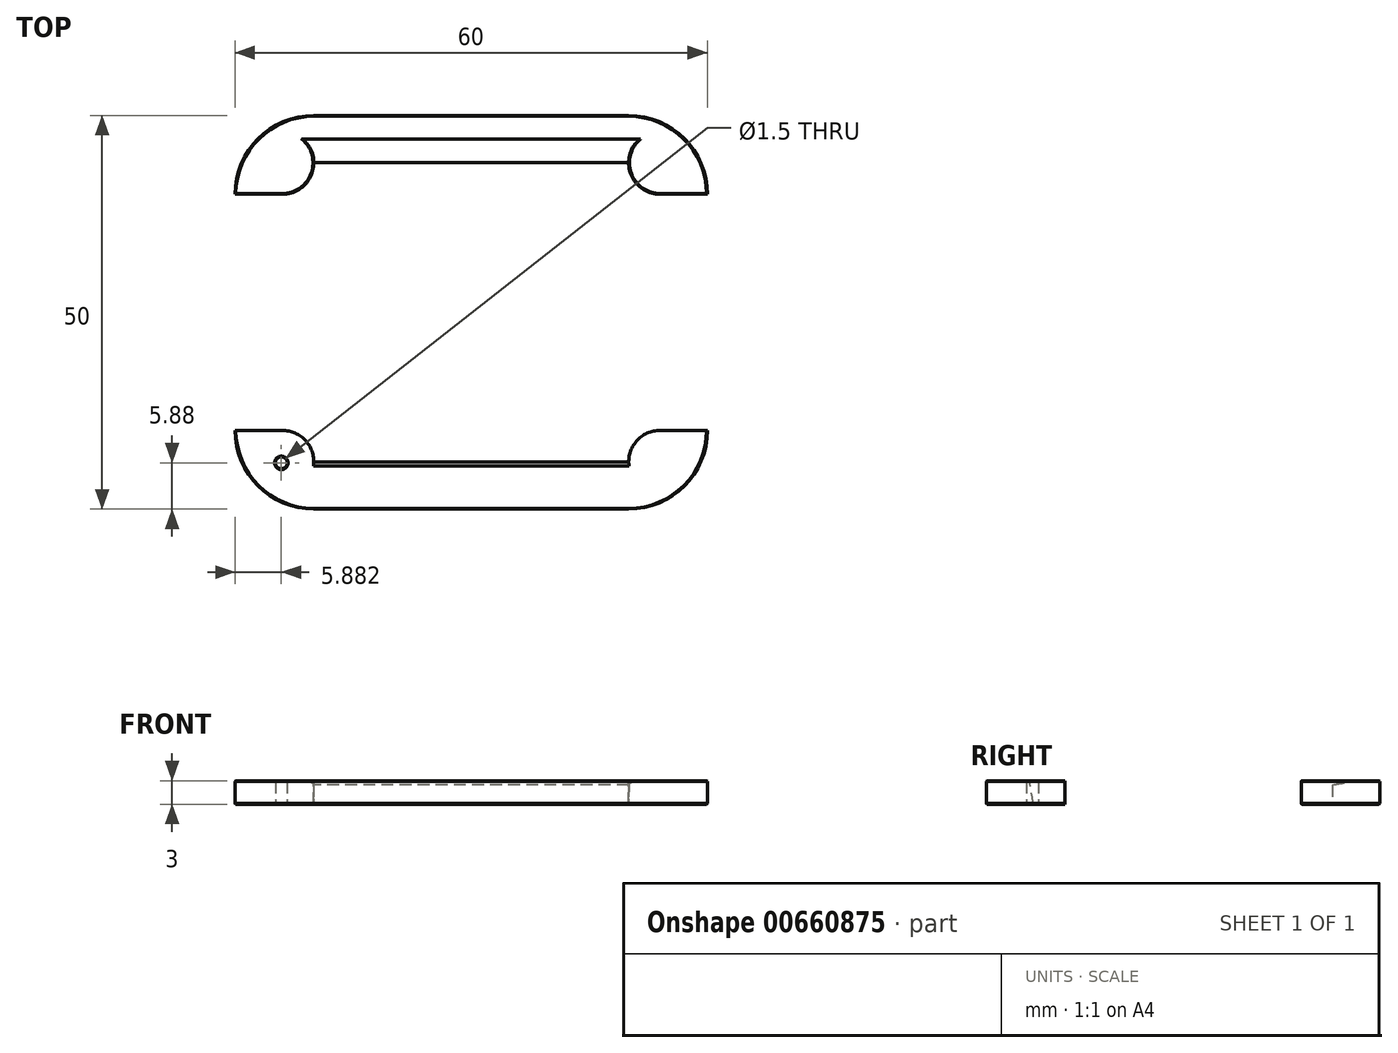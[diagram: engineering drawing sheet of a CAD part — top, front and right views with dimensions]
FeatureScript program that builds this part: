
annotation { "Feature Type Name" : "Feature", "Feature Type Description" : "" }
export const myFeature = defineFeature(function(context is Context, id is Id, definition is map)
    precondition{}
    {
        {
            var Q0;
            Q0=qCreatedBy(makeId("Top.planeOp"),FACE);
            var sketch = newSketch(context, id + "F0", { "sketchPlane" : qUnion([Q0])});
            skLineSegment(sketch, "E0.bottom", {"start": v(-81.76, 14.12) * mm, "end": v(-71.76, 14.12) * mm});
            skLineSegment(sketch, "E0.top", {"start": v(-81.76, 4.12) * mm, "end": v(-71.76, 4.12) * mm});
            skLineSegment(sketch, "E0.left", {"start": v(-81.76, 14.12) * mm, "end": v(-81.76, 4.12) * mm});
            skLineSegment(sketch, "E0.right", {"start": v(-71.76, 14.12) * mm, "end": v(-71.76, 4.12) * mm});
            skLineSegment(sketch, "E1.bottom", {"start": v(-71.76, 14.12) * mm, "end": v(-31.76, 14.12) * mm});
            skLineSegment(sketch, "E1.top", {"start": v(-71.76, 8.12) * mm, "end": v(-31.76, 8.12) * mm});
            skLineSegment(sketch, "E1.left", {"start": v(-71.76, 14.12) * mm, "end": v(-71.76, 8.12) * mm});
            skLineSegment(sketch, "E1.right", {"start": v(-31.76, 14.12) * mm, "end": v(-31.76, 8.12) * mm});
            skLineSegment(sketch, "E2.bottom", {"start": v(-31.76, 14.12) * mm, "end": v(-21.76, 14.12) * mm});
            skLineSegment(sketch, "E2.top", {"start": v(-31.76, 4.12) * mm, "end": v(-21.76, 4.12) * mm});
            skLineSegment(sketch, "E2.left", {"start": v(-31.76, 14.12) * mm, "end": v(-31.76, 4.12) * mm});
            skLineSegment(sketch, "E2.right", {"start": v(-21.76, 14.12) * mm, "end": v(-21.76, 4.12) * mm});
            skLineSegment(sketch, "E3.bottom", {"start": v(-27.76, 4.12) * mm, "end": v(-21.76, 4.12) * mm});
            skLineSegment(sketch, "E3.top", {"start": v(-27.76, -25.88) * mm, "end": v(-21.76, -25.88) * mm});
            skLineSegment(sketch, "E3.left", {"start": v(-27.76, 4.12) * mm, "end": v(-27.76, -25.88) * mm});
            skLineSegment(sketch, "E3.right", {"start": v(-21.76, 4.12) * mm, "end": v(-21.76, -25.88) * mm});
            skLineSegment(sketch, "E4.bottom", {"start": v(-31.76, -25.88) * mm, "end": v(-21.76, -25.88) * mm});
            skLineSegment(sketch, "E4.top", {"start": v(-31.76, -35.88) * mm, "end": v(-21.76, -35.88) * mm});
            skLineSegment(sketch, "E4.left", {"start": v(-31.76, -25.88) * mm, "end": v(-31.76, -35.88) * mm});
            skLineSegment(sketch, "E4.right", {"start": v(-21.76, -25.88) * mm, "end": v(-21.76, -35.88) * mm});
            skLineSegment(sketch, "E5.bottom", {"start": v(-71.76, -29.88) * mm, "end": v(-31.76, -29.88) * mm});
            skLineSegment(sketch, "E5.top", {"start": v(-71.76, -35.88) * mm, "end": v(-31.76, -35.88) * mm});
            skLineSegment(sketch, "E5.left", {"start": v(-71.76, -29.88) * mm, "end": v(-71.76, -35.88) * mm});
            skLineSegment(sketch, "E5.right", {"start": v(-31.76, -29.88) * mm, "end": v(-31.76, -35.88) * mm});
            skLineSegment(sketch, "E6.bottom", {"start": v(-81.76, -25.88) * mm, "end": v(-71.76, -25.88) * mm});
            skLineSegment(sketch, "E6.top", {"start": v(-81.76, -35.88) * mm, "end": v(-71.76, -35.88) * mm});
            skLineSegment(sketch, "E6.left", {"start": v(-81.76, -25.88) * mm, "end": v(-81.76, -35.88) * mm});
            skLineSegment(sketch, "E6.right", {"start": v(-71.76, -25.88) * mm, "end": v(-71.76, -35.88) * mm});
            skLineSegment(sketch, "E7.bottom", {"start": v(-81.76, 4.12) * mm, "end": v(-75.76, 4.12) * mm});
            skLineSegment(sketch, "E7.top", {"start": v(-81.76, -25.88) * mm, "end": v(-75.76, -25.88) * mm});
            skLineSegment(sketch, "E7.left", {"start": v(-81.76, 4.12) * mm, "end": v(-81.76, -25.88) * mm});
            skLineSegment(sketch, "E7.right", {"start": v(-75.76, 4.12) * mm, "end": v(-75.76, -25.88) * mm});
            skCircle(sketch, "E8", {"center": v(-75.88, -30) * mm, "radius": 0.75 * mm});
            skSolve(sketch);
        }
        {
            var Q0;
            Q0=makeQuery(id+"F0.imprint","IMPRINT",FACE,{"disambiguationData":[TD([[makeQuery(id+"F0.imprint","IMPRINT",EDGE,{"derivedFrom":sQuery(id+"F0.wireOp",EDGE,"E0.bottom")}),-1.0]])]});
            var Q1;
            {var subQ0=sQuery(id+"F0.wireOp",EDGE,"E1.bottom");Q1=makeQuery(id+"F0.imprint","IMPRINT",FACE,{"disambiguationData":[TD([[makeQuery(id+"F0.imprint","IMPRINT",EDGE,{"derivedFrom":subQ0}),-1.0]])]});}
            var Q2;
            {var subQ3=sQuery(id+"F0.wireOp",EDGE,"E2.bottom");Q2=makeQuery(id+"F0.imprint","IMPRINT",FACE,{"disambiguationData":[TD([[makeQuery(id+"F0.imprint","IMPRINT",EDGE,{"derivedFrom":subQ3}),-1.0]])]});}
            var Q3;
            Q3=makeQuery(id+"F0.imprint","IMPRINT",FACE,{"disambiguationData":[TD([[makeQuery(id+"F0.imprint","IMPRINT",EDGE,{"derivedFrom":sQuery(id+"F0.wireOp",EDGE,"E3.bottom")}),-1.0]])]});
            var Q4;
            Q4=makeQuery(id+"F0.imprint","IMPRINT",FACE,{"disambiguationData":[TD([[makeQuery(id+"F0.imprint","IMPRINT",EDGE,{"derivedFrom":sQuery(id+"F0.wireOp",EDGE,"E4.top")}),1.0]])]});
            var Q5;
            {var subQ0=sQuery(id+"F0.wireOp",EDGE,"E5.bottom");Q5=makeQuery(id+"F0.imprint","IMPRINT",FACE,{"disambiguationData":[TD([[makeQuery(id+"F0.imprint","IMPRINT",EDGE,{"derivedFrom":subQ0}),-1.0]])]});}
            var Q6;
            {var subQ2=sQuery(id+"F0.wireOp",EDGE,"E6.bottom");Q6=makeQuery(id+"F0.imprint","IMPRINT",FACE,{"disambiguationData":[TD([[makeQuery(id+"F0.imprint","IMPRINT",EDGE,{"derivedFrom":subQ2}),-1.0]])]});}
            var Q7;
            Q7=makeQuery(id+"F0.imprint","IMPRINT",FACE,{"disambiguationData":[TD([[makeQuery(id+"F0.imprint","IMPRINT",EDGE,{"derivedFrom":sQuery(id+"F0.wireOp",EDGE,"E7.bottom")}),-1.0]])]});
            extrude(context, id + "F1", {"entities" : qUnion([Q0, Q1, Q2, Q3, Q4, Q5, Q6, Q7]), "flatOperationType" : FlatOperationType.REMOVE, "depth" : 3 * mm, "offsetDistance" : 25 * mm, "domain" : OperationDomain.MODEL});
        }
        {
            var Q0;
            Q0=makeQuery(id+"F1.opExtrude","SWEPT_EDGE",EDGE,{"disambiguationData":[OSD([sQuery(id+"F0.wireOp",EDGE,"E6.top"),sQuery(id+"F0.wireOp",EDGE,"E6.left")])]});
            var Q1;
            Q1=makeQuery(id+"F1.opExtrude","SWEPT_EDGE",EDGE,{"disambiguationData":[OSD([sQuery(id+"F0.wireOp",EDGE,"E4.top"),sQuery(id+"F0.wireOp",EDGE,"E4.right")])]});
            var Q2;
            Q2=makeQuery(id+"F1.opExtrude","SWEPT_EDGE",EDGE,{"disambiguationData":[OSD([sQuery(id+"F0.wireOp",EDGE,"E2.bottom"),sQuery(id+"F0.wireOp",EDGE,"E2.right")])]});
            var Q3;
            Q3=makeQuery(id+"F1.opExtrude","SWEPT_EDGE",EDGE,{"disambiguationData":[OSD([sQuery(id+"F0.wireOp",EDGE,"E0.bottom"),sQuery(id+"F0.wireOp",EDGE,"E0.left")])]});
            fillet(context, id + "F2", {"entities" : qUnion([Q0, Q1, Q2, Q3]), "radius" : 10 * mm, "tangentPropagation" : true, "defaultsChanged" : false, "vertexSettings" : [], "allowEdgeOverflow" : false});
        }
        {
            var Q0;
            Q0=makeQuery(id+"F1.opExtrude","SWEPT_EDGE",EDGE,{"disambiguationData":[OSD([sQuery(id+"F0.wireOp",EDGE,"E2.top"),sQuery(id+"F0.wireOp",EDGE,"E2.left")])]});
            var Q1;
            Q1=makeQuery(id+"F1.opExtrude","SWEPT_EDGE",EDGE,{"disambiguationData":[OSD([sQuery(id+"F0.wireOp",EDGE,"E0.top"),sQuery(id+"F0.wireOp",EDGE,"E0.right")])]});
            var Q2;
            Q2=makeQuery(id+"F1.opExtrude","SWEPT_EDGE",EDGE,{"disambiguationData":[OSD([sQuery(id+"F0.wireOp",EDGE,"E4.bottom"),sQuery(id+"F0.wireOp",EDGE,"E4.left")])]});
            var Q3;
            Q3=makeQuery(id+"F1.opExtrude","SWEPT_EDGE",EDGE,{"disambiguationData":[OSD([sQuery(id+"F0.wireOp",EDGE,"E6.bottom"),sQuery(id+"F0.wireOp",EDGE,"E6.right")])]});
            fillet(context, id + "F3", {"entities" : qUnion([Q0, Q1, Q2, Q3]), "radius" : 4 * mm, "tangentPropagation" : true, "defaultsChanged" : false, "vertexSettings" : [], "allowEdgeOverflow" : false});
        }
        {
            var Q0;
            Q0=makeQuery(id+"F1.opExtrude","CAP_EDGE",EDGE,{"disambiguationData":[OSD([sQuery(id+"F0.wireOp",EDGE,"E7.right")])],"isStart":false});
            var Q1;
            Q1=makeQuery(id+"F1.opExtrude","CAP_EDGE",EDGE,{"disambiguationData":[OSD([sQuery(id+"F0.wireOp",EDGE,"E1.top")])],"isStart":false});
            var Q2;
            Q2=makeQuery(id+"F1.opExtrude","CAP_EDGE",EDGE,{"disambiguationData":[OSD([sQuery(id+"F0.wireOp",EDGE,"E3.left")])],"isStart":false});
            var Q3;
            Q3=makeQuery(id+"F1.opExtrude","CAP_EDGE",EDGE,{"disambiguationData":[OSD([sQuery(id+"F0.wireOp",EDGE,"E5.bottom")])],"isStart":false});
            chamfer(context, id + "F4", {"entities" : qUnion([Q0, Q1, Q2, Q3]), "chamferType" : ChamferType.OFFSET_ANGLE, "width" : 3 * mm, "oppositeDirection" : false, "angle" : 10 * degree, "tangentPropagation" : true});
        }
        {
            var Q0;
            Q0=makeQuery(id+"F1.opExtrude","CAP_EDGE",EDGE,{"disambiguationData":[OSD([sQuery(id+"F0.wireOp",EDGE,"E0.left"),sQuery(id+"F0.wireOp",EDGE,"E6.left"),sQuery(id+"F0.wireOp",EDGE,"E7.left")])],"isStart":false});
            var Q1;
            {var subQ0=sQuery(id+"F0.wireOp",EDGE,"E0.left");var subQ1=sQuery(id+"F0.wireOp",EDGE,"E0.bottom");Q1=makeQuery(id+"F2.opFillet","BLEND_EDGE",EDGE,{"blendedFrom":[makeQuery(id+"F1.opExtrude","SWEPT_EDGE",EDGE,{"disambiguationData":[OSD([subQ1,subQ0])]}),makeQuery(id+"F1.opExtrude","CAP_FACE",FACE,{"disambiguationData":[OSD([subQ1,sQuery(id+"F0.wireOp",EDGE,"E0.top"),subQ0,sQuery(id+"F0.wireOp",EDGE,"E0.right"),sQuery(id+"F0.wireOp",EDGE,"E1.bottom"),sQuery(id+"F0.wireOp",EDGE,"E1.top"),sQuery(id+"F0.wireOp",EDGE,"E2.bottom"),sQuery(id+"F0.wireOp",EDGE,"E2.top"),sQuery(id+"F0.wireOp",EDGE,"E2.left"),sQuery(id+"F0.wireOp",EDGE,"E2.right"),sQuery(id+"F0.wireOp",EDGE,"E3.left"),sQuery(id+"F0.wireOp",EDGE,"E3.right"),sQuery(id+"F0.wireOp",EDGE,"E4.bottom"),sQuery(id+"F0.wireOp",EDGE,"E4.top"),sQuery(id+"F0.wireOp",EDGE,"E4.left"),sQuery(id+"F0.wireOp",EDGE,"E4.right"),sQuery(id+"F0.wireOp",EDGE,"E5.bottom"),sQuery(id+"F0.wireOp",EDGE,"E5.top"),sQuery(id+"F0.wireOp",EDGE,"E6.bottom"),sQuery(id+"F0.wireOp",EDGE,"E6.top"),sQuery(id+"F0.wireOp",EDGE,"E6.left"),sQuery(id+"F0.wireOp",EDGE,"E6.right"),sQuery(id+"F0.wireOp",EDGE,"E7.left"),sQuery(id+"F0.wireOp",EDGE,"E7.right")])],"isStart":false})],"blendedInto":[makeQuery(id+"F1.opExtrude","CAP_FACE",FACE,{"disambiguationData":[OSD([subQ1,sQuery(id+"F0.wireOp",EDGE,"E0.top"),subQ0,sQuery(id+"F0.wireOp",EDGE,"E0.right"),sQuery(id+"F0.wireOp",EDGE,"E1.bottom"),sQuery(id+"F0.wireOp",EDGE,"E1.top"),sQuery(id+"F0.wireOp",EDGE,"E2.bottom"),sQuery(id+"F0.wireOp",EDGE,"E2.top"),sQuery(id+"F0.wireOp",EDGE,"E2.left"),sQuery(id+"F0.wireOp",EDGE,"E2.right"),sQuery(id+"F0.wireOp",EDGE,"E3.left"),sQuery(id+"F0.wireOp",EDGE,"E3.right"),sQuery(id+"F0.wireOp",EDGE,"E4.bottom"),sQuery(id+"F0.wireOp",EDGE,"E4.top"),sQuery(id+"F0.wireOp",EDGE,"E4.left"),sQuery(id+"F0.wireOp",EDGE,"E4.right"),sQuery(id+"F0.wireOp",EDGE,"E5.bottom"),sQuery(id+"F0.wireOp",EDGE,"E5.top"),sQuery(id+"F0.wireOp",EDGE,"E6.bottom"),sQuery(id+"F0.wireOp",EDGE,"E6.top"),sQuery(id+"F0.wireOp",EDGE,"E6.left"),sQuery(id+"F0.wireOp",EDGE,"E6.right"),sQuery(id+"F0.wireOp",EDGE,"E7.left"),sQuery(id+"F0.wireOp",EDGE,"E7.right")])],"isStart":false})]});}
            var Q2;
            Q2=makeQuery(id+"F1.opExtrude","CAP_EDGE",EDGE,{"disambiguationData":[OSD([sQuery(id+"F0.wireOp",EDGE,"E0.bottom"),sQuery(id+"F0.wireOp",EDGE,"E1.bottom"),sQuery(id+"F0.wireOp",EDGE,"E2.bottom")])],"isStart":false});
            var Q3;
            {var subQ0=sQuery(id+"F0.wireOp",EDGE,"E1.top");Q3=makeQuery(id+"F4.opChamfer","BLEND_EDGE",EDGE,{"blendedFrom":[makeQuery(id+"F1.opExtrude","CAP_EDGE",EDGE,{"disambiguationData":[OSD([subQ0])],"isStart":false}),makeQuery(id+"F1.opExtrude","CAP_FACE",FACE,{"disambiguationData":[OSD([sQuery(id+"F0.wireOp",EDGE,"E0.bottom"),sQuery(id+"F0.wireOp",EDGE,"E0.top"),sQuery(id+"F0.wireOp",EDGE,"E0.left"),sQuery(id+"F0.wireOp",EDGE,"E0.right"),sQuery(id+"F0.wireOp",EDGE,"E1.bottom"),subQ0,sQuery(id+"F0.wireOp",EDGE,"E2.bottom"),sQuery(id+"F0.wireOp",EDGE,"E2.top"),sQuery(id+"F0.wireOp",EDGE,"E2.left"),sQuery(id+"F0.wireOp",EDGE,"E2.right"),sQuery(id+"F0.wireOp",EDGE,"E3.left"),sQuery(id+"F0.wireOp",EDGE,"E3.right"),sQuery(id+"F0.wireOp",EDGE,"E4.bottom"),sQuery(id+"F0.wireOp",EDGE,"E4.top"),sQuery(id+"F0.wireOp",EDGE,"E4.left"),sQuery(id+"F0.wireOp",EDGE,"E4.right"),sQuery(id+"F0.wireOp",EDGE,"E5.bottom"),sQuery(id+"F0.wireOp",EDGE,"E5.top"),sQuery(id+"F0.wireOp",EDGE,"E6.bottom"),sQuery(id+"F0.wireOp",EDGE,"E6.top"),sQuery(id+"F0.wireOp",EDGE,"E6.left"),sQuery(id+"F0.wireOp",EDGE,"E6.right"),sQuery(id+"F0.wireOp",EDGE,"E7.left"),sQuery(id+"F0.wireOp",EDGE,"E7.right")])],"isStart":false})],"blendedInto":[makeQuery(id+"F1.opExtrude","CAP_FACE",FACE,{"disambiguationData":[OSD([sQuery(id+"F0.wireOp",EDGE,"E0.bottom"),sQuery(id+"F0.wireOp",EDGE,"E0.top"),sQuery(id+"F0.wireOp",EDGE,"E0.left"),sQuery(id+"F0.wireOp",EDGE,"E0.right"),sQuery(id+"F0.wireOp",EDGE,"E1.bottom"),subQ0,sQuery(id+"F0.wireOp",EDGE,"E2.bottom"),sQuery(id+"F0.wireOp",EDGE,"E2.top"),sQuery(id+"F0.wireOp",EDGE,"E2.left"),sQuery(id+"F0.wireOp",EDGE,"E2.right"),sQuery(id+"F0.wireOp",EDGE,"E3.left"),sQuery(id+"F0.wireOp",EDGE,"E3.right"),sQuery(id+"F0.wireOp",EDGE,"E4.bottom"),sQuery(id+"F0.wireOp",EDGE,"E4.top"),sQuery(id+"F0.wireOp",EDGE,"E4.left"),sQuery(id+"F0.wireOp",EDGE,"E4.right"),sQuery(id+"F0.wireOp",EDGE,"E5.bottom"),sQuery(id+"F0.wireOp",EDGE,"E5.top"),sQuery(id+"F0.wireOp",EDGE,"E6.bottom"),sQuery(id+"F0.wireOp",EDGE,"E6.top"),sQuery(id+"F0.wireOp",EDGE,"E6.left"),sQuery(id+"F0.wireOp",EDGE,"E6.right"),sQuery(id+"F0.wireOp",EDGE,"E7.left"),sQuery(id+"F0.wireOp",EDGE,"E7.right")])],"isStart":false})]});}
            var Q4;
            {var subQ0=sQuery(id+"F0.wireOp",EDGE,"E7.right");Q4=makeQuery(id+"F4.opChamfer","BLEND_EDGE",EDGE,{"blendedFrom":[makeQuery(id+"F1.opExtrude","CAP_EDGE",EDGE,{"disambiguationData":[OSD([subQ0])],"isStart":false}),makeQuery(id+"F1.opExtrude","CAP_FACE",FACE,{"disambiguationData":[OSD([sQuery(id+"F0.wireOp",EDGE,"E0.bottom"),sQuery(id+"F0.wireOp",EDGE,"E0.top"),sQuery(id+"F0.wireOp",EDGE,"E0.left"),sQuery(id+"F0.wireOp",EDGE,"E0.right"),sQuery(id+"F0.wireOp",EDGE,"E1.bottom"),sQuery(id+"F0.wireOp",EDGE,"E1.top"),sQuery(id+"F0.wireOp",EDGE,"E2.bottom"),sQuery(id+"F0.wireOp",EDGE,"E2.top"),sQuery(id+"F0.wireOp",EDGE,"E2.left"),sQuery(id+"F0.wireOp",EDGE,"E2.right"),sQuery(id+"F0.wireOp",EDGE,"E3.left"),sQuery(id+"F0.wireOp",EDGE,"E3.right"),sQuery(id+"F0.wireOp",EDGE,"E4.bottom"),sQuery(id+"F0.wireOp",EDGE,"E4.top"),sQuery(id+"F0.wireOp",EDGE,"E4.left"),sQuery(id+"F0.wireOp",EDGE,"E4.right"),sQuery(id+"F0.wireOp",EDGE,"E5.bottom"),sQuery(id+"F0.wireOp",EDGE,"E5.top"),sQuery(id+"F0.wireOp",EDGE,"E6.bottom"),sQuery(id+"F0.wireOp",EDGE,"E6.top"),sQuery(id+"F0.wireOp",EDGE,"E6.left"),sQuery(id+"F0.wireOp",EDGE,"E6.right"),sQuery(id+"F0.wireOp",EDGE,"E7.left"),subQ0])],"isStart":false})],"blendedInto":[makeQuery(id+"F1.opExtrude","CAP_FACE",FACE,{"disambiguationData":[OSD([sQuery(id+"F0.wireOp",EDGE,"E0.bottom"),sQuery(id+"F0.wireOp",EDGE,"E0.top"),sQuery(id+"F0.wireOp",EDGE,"E0.left"),sQuery(id+"F0.wireOp",EDGE,"E0.right"),sQuery(id+"F0.wireOp",EDGE,"E1.bottom"),sQuery(id+"F0.wireOp",EDGE,"E1.top"),sQuery(id+"F0.wireOp",EDGE,"E2.bottom"),sQuery(id+"F0.wireOp",EDGE,"E2.top"),sQuery(id+"F0.wireOp",EDGE,"E2.left"),sQuery(id+"F0.wireOp",EDGE,"E2.right"),sQuery(id+"F0.wireOp",EDGE,"E3.left"),sQuery(id+"F0.wireOp",EDGE,"E3.right"),sQuery(id+"F0.wireOp",EDGE,"E4.bottom"),sQuery(id+"F0.wireOp",EDGE,"E4.top"),sQuery(id+"F0.wireOp",EDGE,"E4.left"),sQuery(id+"F0.wireOp",EDGE,"E4.right"),sQuery(id+"F0.wireOp",EDGE,"E5.bottom"),sQuery(id+"F0.wireOp",EDGE,"E5.top"),sQuery(id+"F0.wireOp",EDGE,"E6.bottom"),sQuery(id+"F0.wireOp",EDGE,"E6.top"),sQuery(id+"F0.wireOp",EDGE,"E6.left"),sQuery(id+"F0.wireOp",EDGE,"E6.right"),sQuery(id+"F0.wireOp",EDGE,"E7.left"),subQ0])],"isStart":false})]});}
            var Q5;
            {var subQ0=sQuery(id+"F0.wireOp",EDGE,"E0.right");var subQ1=sQuery(id+"F0.wireOp",EDGE,"E0.top");Q5=makeQuery(id+"F3.opFillet","BLEND_EDGE",EDGE,{"blendedFrom":[makeQuery(id+"F1.opExtrude","SWEPT_EDGE",EDGE,{"disambiguationData":[OSD([subQ1,subQ0])]}),makeQuery(id+"F1.opExtrude","CAP_FACE",FACE,{"disambiguationData":[OSD([sQuery(id+"F0.wireOp",EDGE,"E0.bottom"),subQ1,sQuery(id+"F0.wireOp",EDGE,"E0.left"),subQ0,sQuery(id+"F0.wireOp",EDGE,"E1.bottom"),sQuery(id+"F0.wireOp",EDGE,"E1.top"),sQuery(id+"F0.wireOp",EDGE,"E2.bottom"),sQuery(id+"F0.wireOp",EDGE,"E2.top"),sQuery(id+"F0.wireOp",EDGE,"E2.left"),sQuery(id+"F0.wireOp",EDGE,"E2.right"),sQuery(id+"F0.wireOp",EDGE,"E3.left"),sQuery(id+"F0.wireOp",EDGE,"E3.right"),sQuery(id+"F0.wireOp",EDGE,"E4.bottom"),sQuery(id+"F0.wireOp",EDGE,"E4.top"),sQuery(id+"F0.wireOp",EDGE,"E4.left"),sQuery(id+"F0.wireOp",EDGE,"E4.right"),sQuery(id+"F0.wireOp",EDGE,"E5.bottom"),sQuery(id+"F0.wireOp",EDGE,"E5.top"),sQuery(id+"F0.wireOp",EDGE,"E6.bottom"),sQuery(id+"F0.wireOp",EDGE,"E6.top"),sQuery(id+"F0.wireOp",EDGE,"E6.left"),sQuery(id+"F0.wireOp",EDGE,"E6.right"),sQuery(id+"F0.wireOp",EDGE,"E7.left"),sQuery(id+"F0.wireOp",EDGE,"E7.right")])],"isStart":false})],"blendedInto":[makeQuery(id+"F1.opExtrude","CAP_FACE",FACE,{"disambiguationData":[OSD([sQuery(id+"F0.wireOp",EDGE,"E0.bottom"),subQ1,sQuery(id+"F0.wireOp",EDGE,"E0.left"),subQ0,sQuery(id+"F0.wireOp",EDGE,"E1.bottom"),sQuery(id+"F0.wireOp",EDGE,"E1.top"),sQuery(id+"F0.wireOp",EDGE,"E2.bottom"),sQuery(id+"F0.wireOp",EDGE,"E2.top"),sQuery(id+"F0.wireOp",EDGE,"E2.left"),sQuery(id+"F0.wireOp",EDGE,"E2.right"),sQuery(id+"F0.wireOp",EDGE,"E3.left"),sQuery(id+"F0.wireOp",EDGE,"E3.right"),sQuery(id+"F0.wireOp",EDGE,"E4.bottom"),sQuery(id+"F0.wireOp",EDGE,"E4.top"),sQuery(id+"F0.wireOp",EDGE,"E4.left"),sQuery(id+"F0.wireOp",EDGE,"E4.right"),sQuery(id+"F0.wireOp",EDGE,"E5.bottom"),sQuery(id+"F0.wireOp",EDGE,"E5.top"),sQuery(id+"F0.wireOp",EDGE,"E6.bottom"),sQuery(id+"F0.wireOp",EDGE,"E6.top"),sQuery(id+"F0.wireOp",EDGE,"E6.left"),sQuery(id+"F0.wireOp",EDGE,"E6.right"),sQuery(id+"F0.wireOp",EDGE,"E7.left"),sQuery(id+"F0.wireOp",EDGE,"E7.right")])],"isStart":false})]});}
            var Q6;
            {var subQ0=sQuery(id+"F0.wireOp",EDGE,"E6.right");var subQ1=sQuery(id+"F0.wireOp",EDGE,"E6.bottom");Q6=makeQuery(id+"F3.opFillet","BLEND_EDGE",EDGE,{"blendedFrom":[makeQuery(id+"F1.opExtrude","SWEPT_EDGE",EDGE,{"disambiguationData":[OSD([subQ1,subQ0])]}),makeQuery(id+"F1.opExtrude","CAP_FACE",FACE,{"disambiguationData":[OSD([sQuery(id+"F0.wireOp",EDGE,"E0.bottom"),sQuery(id+"F0.wireOp",EDGE,"E0.top"),sQuery(id+"F0.wireOp",EDGE,"E0.left"),sQuery(id+"F0.wireOp",EDGE,"E0.right"),sQuery(id+"F0.wireOp",EDGE,"E1.bottom"),sQuery(id+"F0.wireOp",EDGE,"E1.top"),sQuery(id+"F0.wireOp",EDGE,"E2.bottom"),sQuery(id+"F0.wireOp",EDGE,"E2.top"),sQuery(id+"F0.wireOp",EDGE,"E2.left"),sQuery(id+"F0.wireOp",EDGE,"E2.right"),sQuery(id+"F0.wireOp",EDGE,"E3.left"),sQuery(id+"F0.wireOp",EDGE,"E3.right"),sQuery(id+"F0.wireOp",EDGE,"E4.bottom"),sQuery(id+"F0.wireOp",EDGE,"E4.top"),sQuery(id+"F0.wireOp",EDGE,"E4.left"),sQuery(id+"F0.wireOp",EDGE,"E4.right"),sQuery(id+"F0.wireOp",EDGE,"E5.bottom"),sQuery(id+"F0.wireOp",EDGE,"E5.top"),subQ1,sQuery(id+"F0.wireOp",EDGE,"E6.top"),sQuery(id+"F0.wireOp",EDGE,"E6.left"),subQ0,sQuery(id+"F0.wireOp",EDGE,"E7.left"),sQuery(id+"F0.wireOp",EDGE,"E7.right")])],"isStart":false})],"blendedInto":[makeQuery(id+"F1.opExtrude","CAP_FACE",FACE,{"disambiguationData":[OSD([sQuery(id+"F0.wireOp",EDGE,"E0.bottom"),sQuery(id+"F0.wireOp",EDGE,"E0.top"),sQuery(id+"F0.wireOp",EDGE,"E0.left"),sQuery(id+"F0.wireOp",EDGE,"E0.right"),sQuery(id+"F0.wireOp",EDGE,"E1.bottom"),sQuery(id+"F0.wireOp",EDGE,"E1.top"),sQuery(id+"F0.wireOp",EDGE,"E2.bottom"),sQuery(id+"F0.wireOp",EDGE,"E2.top"),sQuery(id+"F0.wireOp",EDGE,"E2.left"),sQuery(id+"F0.wireOp",EDGE,"E2.right"),sQuery(id+"F0.wireOp",EDGE,"E3.left"),sQuery(id+"F0.wireOp",EDGE,"E3.right"),sQuery(id+"F0.wireOp",EDGE,"E4.bottom"),sQuery(id+"F0.wireOp",EDGE,"E4.top"),sQuery(id+"F0.wireOp",EDGE,"E4.left"),sQuery(id+"F0.wireOp",EDGE,"E4.right"),sQuery(id+"F0.wireOp",EDGE,"E5.bottom"),sQuery(id+"F0.wireOp",EDGE,"E5.top"),subQ1,sQuery(id+"F0.wireOp",EDGE,"E6.top"),sQuery(id+"F0.wireOp",EDGE,"E6.left"),subQ0,sQuery(id+"F0.wireOp",EDGE,"E7.left"),sQuery(id+"F0.wireOp",EDGE,"E7.right")])],"isStart":false})]});}
            var Q7;
            {var subQ0=sQuery(id+"F0.wireOp",EDGE,"E5.bottom");Q7=makeQuery(id+"F4.opChamfer","BLEND_EDGE",EDGE,{"blendedFrom":[makeQuery(id+"F1.opExtrude","CAP_EDGE",EDGE,{"disambiguationData":[OSD([subQ0])],"isStart":false}),makeQuery(id+"F1.opExtrude","CAP_FACE",FACE,{"disambiguationData":[OSD([sQuery(id+"F0.wireOp",EDGE,"E0.bottom"),sQuery(id+"F0.wireOp",EDGE,"E0.top"),sQuery(id+"F0.wireOp",EDGE,"E0.left"),sQuery(id+"F0.wireOp",EDGE,"E0.right"),sQuery(id+"F0.wireOp",EDGE,"E1.bottom"),sQuery(id+"F0.wireOp",EDGE,"E1.top"),sQuery(id+"F0.wireOp",EDGE,"E2.bottom"),sQuery(id+"F0.wireOp",EDGE,"E2.top"),sQuery(id+"F0.wireOp",EDGE,"E2.left"),sQuery(id+"F0.wireOp",EDGE,"E2.right"),sQuery(id+"F0.wireOp",EDGE,"E3.left"),sQuery(id+"F0.wireOp",EDGE,"E3.right"),sQuery(id+"F0.wireOp",EDGE,"E4.bottom"),sQuery(id+"F0.wireOp",EDGE,"E4.top"),sQuery(id+"F0.wireOp",EDGE,"E4.left"),sQuery(id+"F0.wireOp",EDGE,"E4.right"),subQ0,sQuery(id+"F0.wireOp",EDGE,"E5.top"),sQuery(id+"F0.wireOp",EDGE,"E6.bottom"),sQuery(id+"F0.wireOp",EDGE,"E6.top"),sQuery(id+"F0.wireOp",EDGE,"E6.left"),sQuery(id+"F0.wireOp",EDGE,"E6.right"),sQuery(id+"F0.wireOp",EDGE,"E7.left"),sQuery(id+"F0.wireOp",EDGE,"E7.right")])],"isStart":false})],"blendedInto":[makeQuery(id+"F1.opExtrude","CAP_FACE",FACE,{"disambiguationData":[OSD([sQuery(id+"F0.wireOp",EDGE,"E0.bottom"),sQuery(id+"F0.wireOp",EDGE,"E0.top"),sQuery(id+"F0.wireOp",EDGE,"E0.left"),sQuery(id+"F0.wireOp",EDGE,"E0.right"),sQuery(id+"F0.wireOp",EDGE,"E1.bottom"),sQuery(id+"F0.wireOp",EDGE,"E1.top"),sQuery(id+"F0.wireOp",EDGE,"E2.bottom"),sQuery(id+"F0.wireOp",EDGE,"E2.top"),sQuery(id+"F0.wireOp",EDGE,"E2.left"),sQuery(id+"F0.wireOp",EDGE,"E2.right"),sQuery(id+"F0.wireOp",EDGE,"E3.left"),sQuery(id+"F0.wireOp",EDGE,"E3.right"),sQuery(id+"F0.wireOp",EDGE,"E4.bottom"),sQuery(id+"F0.wireOp",EDGE,"E4.top"),sQuery(id+"F0.wireOp",EDGE,"E4.left"),sQuery(id+"F0.wireOp",EDGE,"E4.right"),subQ0,sQuery(id+"F0.wireOp",EDGE,"E5.top"),sQuery(id+"F0.wireOp",EDGE,"E6.bottom"),sQuery(id+"F0.wireOp",EDGE,"E6.top"),sQuery(id+"F0.wireOp",EDGE,"E6.left"),sQuery(id+"F0.wireOp",EDGE,"E6.right"),sQuery(id+"F0.wireOp",EDGE,"E7.left"),sQuery(id+"F0.wireOp",EDGE,"E7.right")])],"isStart":false})]});}
            var Q8;
            {var subQ0=sQuery(id+"F0.wireOp",EDGE,"E4.left");var subQ1=sQuery(id+"F0.wireOp",EDGE,"E4.bottom");Q8=makeQuery(id+"F3.opFillet","BLEND_EDGE",EDGE,{"blendedFrom":[makeQuery(id+"F1.opExtrude","SWEPT_EDGE",EDGE,{"disambiguationData":[OSD([subQ1,subQ0])]}),makeQuery(id+"F1.opExtrude","CAP_FACE",FACE,{"disambiguationData":[OSD([sQuery(id+"F0.wireOp",EDGE,"E0.bottom"),sQuery(id+"F0.wireOp",EDGE,"E0.top"),sQuery(id+"F0.wireOp",EDGE,"E0.left"),sQuery(id+"F0.wireOp",EDGE,"E0.right"),sQuery(id+"F0.wireOp",EDGE,"E1.bottom"),sQuery(id+"F0.wireOp",EDGE,"E1.top"),sQuery(id+"F0.wireOp",EDGE,"E2.bottom"),sQuery(id+"F0.wireOp",EDGE,"E2.top"),sQuery(id+"F0.wireOp",EDGE,"E2.left"),sQuery(id+"F0.wireOp",EDGE,"E2.right"),sQuery(id+"F0.wireOp",EDGE,"E3.left"),sQuery(id+"F0.wireOp",EDGE,"E3.right"),subQ1,sQuery(id+"F0.wireOp",EDGE,"E4.top"),subQ0,sQuery(id+"F0.wireOp",EDGE,"E4.right"),sQuery(id+"F0.wireOp",EDGE,"E5.bottom"),sQuery(id+"F0.wireOp",EDGE,"E5.top"),sQuery(id+"F0.wireOp",EDGE,"E6.bottom"),sQuery(id+"F0.wireOp",EDGE,"E6.top"),sQuery(id+"F0.wireOp",EDGE,"E6.left"),sQuery(id+"F0.wireOp",EDGE,"E6.right"),sQuery(id+"F0.wireOp",EDGE,"E7.left"),sQuery(id+"F0.wireOp",EDGE,"E7.right")])],"isStart":false})],"blendedInto":[makeQuery(id+"F1.opExtrude","CAP_FACE",FACE,{"disambiguationData":[OSD([sQuery(id+"F0.wireOp",EDGE,"E0.bottom"),sQuery(id+"F0.wireOp",EDGE,"E0.top"),sQuery(id+"F0.wireOp",EDGE,"E0.left"),sQuery(id+"F0.wireOp",EDGE,"E0.right"),sQuery(id+"F0.wireOp",EDGE,"E1.bottom"),sQuery(id+"F0.wireOp",EDGE,"E1.top"),sQuery(id+"F0.wireOp",EDGE,"E2.bottom"),sQuery(id+"F0.wireOp",EDGE,"E2.top"),sQuery(id+"F0.wireOp",EDGE,"E2.left"),sQuery(id+"F0.wireOp",EDGE,"E2.right"),sQuery(id+"F0.wireOp",EDGE,"E3.left"),sQuery(id+"F0.wireOp",EDGE,"E3.right"),subQ1,sQuery(id+"F0.wireOp",EDGE,"E4.top"),subQ0,sQuery(id+"F0.wireOp",EDGE,"E4.right"),sQuery(id+"F0.wireOp",EDGE,"E5.bottom"),sQuery(id+"F0.wireOp",EDGE,"E5.top"),sQuery(id+"F0.wireOp",EDGE,"E6.bottom"),sQuery(id+"F0.wireOp",EDGE,"E6.top"),sQuery(id+"F0.wireOp",EDGE,"E6.left"),sQuery(id+"F0.wireOp",EDGE,"E6.right"),sQuery(id+"F0.wireOp",EDGE,"E7.left"),sQuery(id+"F0.wireOp",EDGE,"E7.right")])],"isStart":false})]});}
            var Q9;
            {var subQ0=sQuery(id+"F0.wireOp",EDGE,"E3.left");Q9=makeQuery(id+"F4.opChamfer","BLEND_EDGE",EDGE,{"blendedFrom":[makeQuery(id+"F1.opExtrude","CAP_EDGE",EDGE,{"disambiguationData":[OSD([subQ0])],"isStart":false}),makeQuery(id+"F1.opExtrude","CAP_FACE",FACE,{"disambiguationData":[OSD([sQuery(id+"F0.wireOp",EDGE,"E0.bottom"),sQuery(id+"F0.wireOp",EDGE,"E0.top"),sQuery(id+"F0.wireOp",EDGE,"E0.left"),sQuery(id+"F0.wireOp",EDGE,"E0.right"),sQuery(id+"F0.wireOp",EDGE,"E1.bottom"),sQuery(id+"F0.wireOp",EDGE,"E1.top"),sQuery(id+"F0.wireOp",EDGE,"E2.bottom"),sQuery(id+"F0.wireOp",EDGE,"E2.top"),sQuery(id+"F0.wireOp",EDGE,"E2.left"),sQuery(id+"F0.wireOp",EDGE,"E2.right"),subQ0,sQuery(id+"F0.wireOp",EDGE,"E3.right"),sQuery(id+"F0.wireOp",EDGE,"E4.bottom"),sQuery(id+"F0.wireOp",EDGE,"E4.top"),sQuery(id+"F0.wireOp",EDGE,"E4.left"),sQuery(id+"F0.wireOp",EDGE,"E4.right"),sQuery(id+"F0.wireOp",EDGE,"E5.bottom"),sQuery(id+"F0.wireOp",EDGE,"E5.top"),sQuery(id+"F0.wireOp",EDGE,"E6.bottom"),sQuery(id+"F0.wireOp",EDGE,"E6.top"),sQuery(id+"F0.wireOp",EDGE,"E6.left"),sQuery(id+"F0.wireOp",EDGE,"E6.right"),sQuery(id+"F0.wireOp",EDGE,"E7.left"),sQuery(id+"F0.wireOp",EDGE,"E7.right")])],"isStart":false})],"blendedInto":[makeQuery(id+"F1.opExtrude","CAP_FACE",FACE,{"disambiguationData":[OSD([sQuery(id+"F0.wireOp",EDGE,"E0.bottom"),sQuery(id+"F0.wireOp",EDGE,"E0.top"),sQuery(id+"F0.wireOp",EDGE,"E0.left"),sQuery(id+"F0.wireOp",EDGE,"E0.right"),sQuery(id+"F0.wireOp",EDGE,"E1.bottom"),sQuery(id+"F0.wireOp",EDGE,"E1.top"),sQuery(id+"F0.wireOp",EDGE,"E2.bottom"),sQuery(id+"F0.wireOp",EDGE,"E2.top"),sQuery(id+"F0.wireOp",EDGE,"E2.left"),sQuery(id+"F0.wireOp",EDGE,"E2.right"),subQ0,sQuery(id+"F0.wireOp",EDGE,"E3.right"),sQuery(id+"F0.wireOp",EDGE,"E4.bottom"),sQuery(id+"F0.wireOp",EDGE,"E4.top"),sQuery(id+"F0.wireOp",EDGE,"E4.left"),sQuery(id+"F0.wireOp",EDGE,"E4.right"),sQuery(id+"F0.wireOp",EDGE,"E5.bottom"),sQuery(id+"F0.wireOp",EDGE,"E5.top"),sQuery(id+"F0.wireOp",EDGE,"E6.bottom"),sQuery(id+"F0.wireOp",EDGE,"E6.top"),sQuery(id+"F0.wireOp",EDGE,"E6.left"),sQuery(id+"F0.wireOp",EDGE,"E6.right"),sQuery(id+"F0.wireOp",EDGE,"E7.left"),sQuery(id+"F0.wireOp",EDGE,"E7.right")])],"isStart":false})]});}
            var Q10;
            {var subQ0=sQuery(id+"F0.wireOp",EDGE,"E2.left");var subQ1=sQuery(id+"F0.wireOp",EDGE,"E2.top");Q10=makeQuery(id+"F3.opFillet","BLEND_EDGE",EDGE,{"blendedFrom":[makeQuery(id+"F1.opExtrude","SWEPT_EDGE",EDGE,{"disambiguationData":[OSD([subQ1,subQ0])]}),makeQuery(id+"F1.opExtrude","CAP_FACE",FACE,{"disambiguationData":[OSD([sQuery(id+"F0.wireOp",EDGE,"E0.bottom"),sQuery(id+"F0.wireOp",EDGE,"E0.top"),sQuery(id+"F0.wireOp",EDGE,"E0.left"),sQuery(id+"F0.wireOp",EDGE,"E0.right"),sQuery(id+"F0.wireOp",EDGE,"E1.bottom"),sQuery(id+"F0.wireOp",EDGE,"E1.top"),sQuery(id+"F0.wireOp",EDGE,"E2.bottom"),subQ1,subQ0,sQuery(id+"F0.wireOp",EDGE,"E2.right"),sQuery(id+"F0.wireOp",EDGE,"E3.left"),sQuery(id+"F0.wireOp",EDGE,"E3.right"),sQuery(id+"F0.wireOp",EDGE,"E4.bottom"),sQuery(id+"F0.wireOp",EDGE,"E4.top"),sQuery(id+"F0.wireOp",EDGE,"E4.left"),sQuery(id+"F0.wireOp",EDGE,"E4.right"),sQuery(id+"F0.wireOp",EDGE,"E5.bottom"),sQuery(id+"F0.wireOp",EDGE,"E5.top"),sQuery(id+"F0.wireOp",EDGE,"E6.bottom"),sQuery(id+"F0.wireOp",EDGE,"E6.top"),sQuery(id+"F0.wireOp",EDGE,"E6.left"),sQuery(id+"F0.wireOp",EDGE,"E6.right"),sQuery(id+"F0.wireOp",EDGE,"E7.left"),sQuery(id+"F0.wireOp",EDGE,"E7.right")])],"isStart":false})],"blendedInto":[makeQuery(id+"F1.opExtrude","CAP_FACE",FACE,{"disambiguationData":[OSD([sQuery(id+"F0.wireOp",EDGE,"E0.bottom"),sQuery(id+"F0.wireOp",EDGE,"E0.top"),sQuery(id+"F0.wireOp",EDGE,"E0.left"),sQuery(id+"F0.wireOp",EDGE,"E0.right"),sQuery(id+"F0.wireOp",EDGE,"E1.bottom"),sQuery(id+"F0.wireOp",EDGE,"E1.top"),sQuery(id+"F0.wireOp",EDGE,"E2.bottom"),subQ1,subQ0,sQuery(id+"F0.wireOp",EDGE,"E2.right"),sQuery(id+"F0.wireOp",EDGE,"E3.left"),sQuery(id+"F0.wireOp",EDGE,"E3.right"),sQuery(id+"F0.wireOp",EDGE,"E4.bottom"),sQuery(id+"F0.wireOp",EDGE,"E4.top"),sQuery(id+"F0.wireOp",EDGE,"E4.left"),sQuery(id+"F0.wireOp",EDGE,"E4.right"),sQuery(id+"F0.wireOp",EDGE,"E5.bottom"),sQuery(id+"F0.wireOp",EDGE,"E5.top"),sQuery(id+"F0.wireOp",EDGE,"E6.bottom"),sQuery(id+"F0.wireOp",EDGE,"E6.top"),sQuery(id+"F0.wireOp",EDGE,"E6.left"),sQuery(id+"F0.wireOp",EDGE,"E6.right"),sQuery(id+"F0.wireOp",EDGE,"E7.left"),sQuery(id+"F0.wireOp",EDGE,"E7.right")])],"isStart":false})]});}
            var Q11;
            {var subQ0=sQuery(id+"F0.wireOp",EDGE,"E2.right");var subQ1=sQuery(id+"F0.wireOp",EDGE,"E2.bottom");Q11=makeQuery(id+"F2.opFillet","BLEND_EDGE",EDGE,{"blendedFrom":[makeQuery(id+"F1.opExtrude","SWEPT_EDGE",EDGE,{"disambiguationData":[OSD([subQ1,subQ0])]}),makeQuery(id+"F1.opExtrude","CAP_FACE",FACE,{"disambiguationData":[OSD([sQuery(id+"F0.wireOp",EDGE,"E0.bottom"),sQuery(id+"F0.wireOp",EDGE,"E0.top"),sQuery(id+"F0.wireOp",EDGE,"E0.left"),sQuery(id+"F0.wireOp",EDGE,"E0.right"),sQuery(id+"F0.wireOp",EDGE,"E1.bottom"),sQuery(id+"F0.wireOp",EDGE,"E1.top"),subQ1,sQuery(id+"F0.wireOp",EDGE,"E2.top"),sQuery(id+"F0.wireOp",EDGE,"E2.left"),subQ0,sQuery(id+"F0.wireOp",EDGE,"E3.left"),sQuery(id+"F0.wireOp",EDGE,"E3.right"),sQuery(id+"F0.wireOp",EDGE,"E4.bottom"),sQuery(id+"F0.wireOp",EDGE,"E4.top"),sQuery(id+"F0.wireOp",EDGE,"E4.left"),sQuery(id+"F0.wireOp",EDGE,"E4.right"),sQuery(id+"F0.wireOp",EDGE,"E5.bottom"),sQuery(id+"F0.wireOp",EDGE,"E5.top"),sQuery(id+"F0.wireOp",EDGE,"E6.bottom"),sQuery(id+"F0.wireOp",EDGE,"E6.top"),sQuery(id+"F0.wireOp",EDGE,"E6.left"),sQuery(id+"F0.wireOp",EDGE,"E6.right"),sQuery(id+"F0.wireOp",EDGE,"E7.left"),sQuery(id+"F0.wireOp",EDGE,"E7.right")])],"isStart":false})],"blendedInto":[makeQuery(id+"F1.opExtrude","CAP_FACE",FACE,{"disambiguationData":[OSD([sQuery(id+"F0.wireOp",EDGE,"E0.bottom"),sQuery(id+"F0.wireOp",EDGE,"E0.top"),sQuery(id+"F0.wireOp",EDGE,"E0.left"),sQuery(id+"F0.wireOp",EDGE,"E0.right"),sQuery(id+"F0.wireOp",EDGE,"E1.bottom"),sQuery(id+"F0.wireOp",EDGE,"E1.top"),subQ1,sQuery(id+"F0.wireOp",EDGE,"E2.top"),sQuery(id+"F0.wireOp",EDGE,"E2.left"),subQ0,sQuery(id+"F0.wireOp",EDGE,"E3.left"),sQuery(id+"F0.wireOp",EDGE,"E3.right"),sQuery(id+"F0.wireOp",EDGE,"E4.bottom"),sQuery(id+"F0.wireOp",EDGE,"E4.top"),sQuery(id+"F0.wireOp",EDGE,"E4.left"),sQuery(id+"F0.wireOp",EDGE,"E4.right"),sQuery(id+"F0.wireOp",EDGE,"E5.bottom"),sQuery(id+"F0.wireOp",EDGE,"E5.top"),sQuery(id+"F0.wireOp",EDGE,"E6.bottom"),sQuery(id+"F0.wireOp",EDGE,"E6.top"),sQuery(id+"F0.wireOp",EDGE,"E6.left"),sQuery(id+"F0.wireOp",EDGE,"E6.right"),sQuery(id+"F0.wireOp",EDGE,"E7.left"),sQuery(id+"F0.wireOp",EDGE,"E7.right")])],"isStart":false})]});}
            var Q12;
            Q12=makeQuery(id+"F1.opExtrude","CAP_EDGE",EDGE,{"disambiguationData":[OSD([sQuery(id+"F0.wireOp",EDGE,"E2.right"),sQuery(id+"F0.wireOp",EDGE,"E3.right"),sQuery(id+"F0.wireOp",EDGE,"E4.right")])],"isStart":true});
            var Q13;
            Q13=makeQuery(id+"F1.opExtrude","CAP_EDGE",EDGE,{"disambiguationData":[OSD([sQuery(id+"F0.wireOp",EDGE,"E2.right"),sQuery(id+"F0.wireOp",EDGE,"E3.right"),sQuery(id+"F0.wireOp",EDGE,"E4.right")])],"isStart":false});
            var Q14;
            {var subQ0=sQuery(id+"F0.wireOp",EDGE,"E4.right");var subQ1=sQuery(id+"F0.wireOp",EDGE,"E4.top");Q14=makeQuery(id+"F2.opFillet","BLEND_EDGE",EDGE,{"blendedFrom":[makeQuery(id+"F1.opExtrude","SWEPT_EDGE",EDGE,{"disambiguationData":[OSD([subQ1,subQ0])]}),makeQuery(id+"F1.opExtrude","CAP_FACE",FACE,{"disambiguationData":[OSD([sQuery(id+"F0.wireOp",EDGE,"E0.bottom"),sQuery(id+"F0.wireOp",EDGE,"E0.top"),sQuery(id+"F0.wireOp",EDGE,"E0.left"),sQuery(id+"F0.wireOp",EDGE,"E0.right"),sQuery(id+"F0.wireOp",EDGE,"E1.bottom"),sQuery(id+"F0.wireOp",EDGE,"E1.top"),sQuery(id+"F0.wireOp",EDGE,"E2.bottom"),sQuery(id+"F0.wireOp",EDGE,"E2.top"),sQuery(id+"F0.wireOp",EDGE,"E2.left"),sQuery(id+"F0.wireOp",EDGE,"E2.right"),sQuery(id+"F0.wireOp",EDGE,"E3.left"),sQuery(id+"F0.wireOp",EDGE,"E3.right"),sQuery(id+"F0.wireOp",EDGE,"E4.bottom"),subQ1,sQuery(id+"F0.wireOp",EDGE,"E4.left"),subQ0,sQuery(id+"F0.wireOp",EDGE,"E5.bottom"),sQuery(id+"F0.wireOp",EDGE,"E5.top"),sQuery(id+"F0.wireOp",EDGE,"E6.bottom"),sQuery(id+"F0.wireOp",EDGE,"E6.top"),sQuery(id+"F0.wireOp",EDGE,"E6.left"),sQuery(id+"F0.wireOp",EDGE,"E6.right"),sQuery(id+"F0.wireOp",EDGE,"E7.left"),sQuery(id+"F0.wireOp",EDGE,"E7.right")])],"isStart":false})],"blendedInto":[makeQuery(id+"F1.opExtrude","CAP_FACE",FACE,{"disambiguationData":[OSD([sQuery(id+"F0.wireOp",EDGE,"E0.bottom"),sQuery(id+"F0.wireOp",EDGE,"E0.top"),sQuery(id+"F0.wireOp",EDGE,"E0.left"),sQuery(id+"F0.wireOp",EDGE,"E0.right"),sQuery(id+"F0.wireOp",EDGE,"E1.bottom"),sQuery(id+"F0.wireOp",EDGE,"E1.top"),sQuery(id+"F0.wireOp",EDGE,"E2.bottom"),sQuery(id+"F0.wireOp",EDGE,"E2.top"),sQuery(id+"F0.wireOp",EDGE,"E2.left"),sQuery(id+"F0.wireOp",EDGE,"E2.right"),sQuery(id+"F0.wireOp",EDGE,"E3.left"),sQuery(id+"F0.wireOp",EDGE,"E3.right"),sQuery(id+"F0.wireOp",EDGE,"E4.bottom"),subQ1,sQuery(id+"F0.wireOp",EDGE,"E4.left"),subQ0,sQuery(id+"F0.wireOp",EDGE,"E5.bottom"),sQuery(id+"F0.wireOp",EDGE,"E5.top"),sQuery(id+"F0.wireOp",EDGE,"E6.bottom"),sQuery(id+"F0.wireOp",EDGE,"E6.top"),sQuery(id+"F0.wireOp",EDGE,"E6.left"),sQuery(id+"F0.wireOp",EDGE,"E6.right"),sQuery(id+"F0.wireOp",EDGE,"E7.left"),sQuery(id+"F0.wireOp",EDGE,"E7.right")])],"isStart":false})]});}
            var Q15;
            Q15=makeQuery(id+"F1.opExtrude","CAP_EDGE",EDGE,{"disambiguationData":[OSD([sQuery(id+"F0.wireOp",EDGE,"E4.top"),sQuery(id+"F0.wireOp",EDGE,"E5.top"),sQuery(id+"F0.wireOp",EDGE,"E6.top")])],"isStart":false});
            var Q16;
            {var subQ0=sQuery(id+"F0.wireOp",EDGE,"E6.left");var subQ1=sQuery(id+"F0.wireOp",EDGE,"E6.top");Q16=makeQuery(id+"F2.opFillet","BLEND_EDGE",EDGE,{"blendedFrom":[makeQuery(id+"F1.opExtrude","SWEPT_EDGE",EDGE,{"disambiguationData":[OSD([subQ1,subQ0])]}),makeQuery(id+"F1.opExtrude","CAP_FACE",FACE,{"disambiguationData":[OSD([sQuery(id+"F0.wireOp",EDGE,"E0.bottom"),sQuery(id+"F0.wireOp",EDGE,"E0.top"),sQuery(id+"F0.wireOp",EDGE,"E0.left"),sQuery(id+"F0.wireOp",EDGE,"E0.right"),sQuery(id+"F0.wireOp",EDGE,"E1.bottom"),sQuery(id+"F0.wireOp",EDGE,"E1.top"),sQuery(id+"F0.wireOp",EDGE,"E2.bottom"),sQuery(id+"F0.wireOp",EDGE,"E2.top"),sQuery(id+"F0.wireOp",EDGE,"E2.left"),sQuery(id+"F0.wireOp",EDGE,"E2.right"),sQuery(id+"F0.wireOp",EDGE,"E3.left"),sQuery(id+"F0.wireOp",EDGE,"E3.right"),sQuery(id+"F0.wireOp",EDGE,"E4.bottom"),sQuery(id+"F0.wireOp",EDGE,"E4.top"),sQuery(id+"F0.wireOp",EDGE,"E4.left"),sQuery(id+"F0.wireOp",EDGE,"E4.right"),sQuery(id+"F0.wireOp",EDGE,"E5.bottom"),sQuery(id+"F0.wireOp",EDGE,"E5.top"),sQuery(id+"F0.wireOp",EDGE,"E6.bottom"),subQ1,subQ0,sQuery(id+"F0.wireOp",EDGE,"E6.right"),sQuery(id+"F0.wireOp",EDGE,"E7.left"),sQuery(id+"F0.wireOp",EDGE,"E7.right")])],"isStart":false})],"blendedInto":[makeQuery(id+"F1.opExtrude","CAP_FACE",FACE,{"disambiguationData":[OSD([sQuery(id+"F0.wireOp",EDGE,"E0.bottom"),sQuery(id+"F0.wireOp",EDGE,"E0.top"),sQuery(id+"F0.wireOp",EDGE,"E0.left"),sQuery(id+"F0.wireOp",EDGE,"E0.right"),sQuery(id+"F0.wireOp",EDGE,"E1.bottom"),sQuery(id+"F0.wireOp",EDGE,"E1.top"),sQuery(id+"F0.wireOp",EDGE,"E2.bottom"),sQuery(id+"F0.wireOp",EDGE,"E2.top"),sQuery(id+"F0.wireOp",EDGE,"E2.left"),sQuery(id+"F0.wireOp",EDGE,"E2.right"),sQuery(id+"F0.wireOp",EDGE,"E3.left"),sQuery(id+"F0.wireOp",EDGE,"E3.right"),sQuery(id+"F0.wireOp",EDGE,"E4.bottom"),sQuery(id+"F0.wireOp",EDGE,"E4.top"),sQuery(id+"F0.wireOp",EDGE,"E4.left"),sQuery(id+"F0.wireOp",EDGE,"E4.right"),sQuery(id+"F0.wireOp",EDGE,"E5.bottom"),sQuery(id+"F0.wireOp",EDGE,"E5.top"),sQuery(id+"F0.wireOp",EDGE,"E6.bottom"),subQ1,subQ0,sQuery(id+"F0.wireOp",EDGE,"E6.right"),sQuery(id+"F0.wireOp",EDGE,"E7.left"),sQuery(id+"F0.wireOp",EDGE,"E7.right")])],"isStart":false})]});}
            var Q17;
            {var subQ0=sQuery(id+"F0.wireOp",EDGE,"E2.right");var subQ1=sQuery(id+"F0.wireOp",EDGE,"E2.bottom");Q17=makeQuery(id+"F2.opFillet","BLEND_EDGE",EDGE,{"blendedFrom":[makeQuery(id+"F1.opExtrude","SWEPT_EDGE",EDGE,{"disambiguationData":[OSD([subQ1,subQ0])]}),makeQuery(id+"F1.opExtrude","CAP_FACE",FACE,{"disambiguationData":[OSD([sQuery(id+"F0.wireOp",EDGE,"E0.bottom"),sQuery(id+"F0.wireOp",EDGE,"E0.top"),sQuery(id+"F0.wireOp",EDGE,"E0.left"),sQuery(id+"F0.wireOp",EDGE,"E0.right"),sQuery(id+"F0.wireOp",EDGE,"E1.bottom"),sQuery(id+"F0.wireOp",EDGE,"E1.top"),subQ1,sQuery(id+"F0.wireOp",EDGE,"E2.top"),sQuery(id+"F0.wireOp",EDGE,"E2.left"),subQ0,sQuery(id+"F0.wireOp",EDGE,"E3.left"),sQuery(id+"F0.wireOp",EDGE,"E3.right"),sQuery(id+"F0.wireOp",EDGE,"E4.bottom"),sQuery(id+"F0.wireOp",EDGE,"E4.top"),sQuery(id+"F0.wireOp",EDGE,"E4.left"),sQuery(id+"F0.wireOp",EDGE,"E4.right"),sQuery(id+"F0.wireOp",EDGE,"E5.bottom"),sQuery(id+"F0.wireOp",EDGE,"E5.top"),sQuery(id+"F0.wireOp",EDGE,"E6.bottom"),sQuery(id+"F0.wireOp",EDGE,"E6.top"),sQuery(id+"F0.wireOp",EDGE,"E6.left"),sQuery(id+"F0.wireOp",EDGE,"E6.right"),sQuery(id+"F0.wireOp",EDGE,"E7.left"),sQuery(id+"F0.wireOp",EDGE,"E7.right")])],"isStart":true})],"blendedInto":[makeQuery(id+"F1.opExtrude","CAP_FACE",FACE,{"disambiguationData":[OSD([sQuery(id+"F0.wireOp",EDGE,"E0.bottom"),sQuery(id+"F0.wireOp",EDGE,"E0.top"),sQuery(id+"F0.wireOp",EDGE,"E0.left"),sQuery(id+"F0.wireOp",EDGE,"E0.right"),sQuery(id+"F0.wireOp",EDGE,"E1.bottom"),sQuery(id+"F0.wireOp",EDGE,"E1.top"),subQ1,sQuery(id+"F0.wireOp",EDGE,"E2.top"),sQuery(id+"F0.wireOp",EDGE,"E2.left"),subQ0,sQuery(id+"F0.wireOp",EDGE,"E3.left"),sQuery(id+"F0.wireOp",EDGE,"E3.right"),sQuery(id+"F0.wireOp",EDGE,"E4.bottom"),sQuery(id+"F0.wireOp",EDGE,"E4.top"),sQuery(id+"F0.wireOp",EDGE,"E4.left"),sQuery(id+"F0.wireOp",EDGE,"E4.right"),sQuery(id+"F0.wireOp",EDGE,"E5.bottom"),sQuery(id+"F0.wireOp",EDGE,"E5.top"),sQuery(id+"F0.wireOp",EDGE,"E6.bottom"),sQuery(id+"F0.wireOp",EDGE,"E6.top"),sQuery(id+"F0.wireOp",EDGE,"E6.left"),sQuery(id+"F0.wireOp",EDGE,"E6.right"),sQuery(id+"F0.wireOp",EDGE,"E7.left"),sQuery(id+"F0.wireOp",EDGE,"E7.right")])],"isStart":true})]});}
            var Q18;
            Q18=makeQuery(id+"F1.opExtrude","CAP_EDGE",EDGE,{"disambiguationData":[OSD([sQuery(id+"F0.wireOp",EDGE,"E0.bottom"),sQuery(id+"F0.wireOp",EDGE,"E1.bottom"),sQuery(id+"F0.wireOp",EDGE,"E2.bottom")])],"isStart":true});
            var Q19;
            {var subQ0=sQuery(id+"F0.wireOp",EDGE,"E0.left");var subQ1=sQuery(id+"F0.wireOp",EDGE,"E0.bottom");Q19=makeQuery(id+"F2.opFillet","BLEND_EDGE",EDGE,{"blendedFrom":[makeQuery(id+"F1.opExtrude","SWEPT_EDGE",EDGE,{"disambiguationData":[OSD([subQ1,subQ0])]}),makeQuery(id+"F1.opExtrude","CAP_FACE",FACE,{"disambiguationData":[OSD([subQ1,sQuery(id+"F0.wireOp",EDGE,"E0.top"),subQ0,sQuery(id+"F0.wireOp",EDGE,"E0.right"),sQuery(id+"F0.wireOp",EDGE,"E1.bottom"),sQuery(id+"F0.wireOp",EDGE,"E1.top"),sQuery(id+"F0.wireOp",EDGE,"E2.bottom"),sQuery(id+"F0.wireOp",EDGE,"E2.top"),sQuery(id+"F0.wireOp",EDGE,"E2.left"),sQuery(id+"F0.wireOp",EDGE,"E2.right"),sQuery(id+"F0.wireOp",EDGE,"E3.left"),sQuery(id+"F0.wireOp",EDGE,"E3.right"),sQuery(id+"F0.wireOp",EDGE,"E4.bottom"),sQuery(id+"F0.wireOp",EDGE,"E4.top"),sQuery(id+"F0.wireOp",EDGE,"E4.left"),sQuery(id+"F0.wireOp",EDGE,"E4.right"),sQuery(id+"F0.wireOp",EDGE,"E5.bottom"),sQuery(id+"F0.wireOp",EDGE,"E5.top"),sQuery(id+"F0.wireOp",EDGE,"E6.bottom"),sQuery(id+"F0.wireOp",EDGE,"E6.top"),sQuery(id+"F0.wireOp",EDGE,"E6.left"),sQuery(id+"F0.wireOp",EDGE,"E6.right"),sQuery(id+"F0.wireOp",EDGE,"E7.left"),sQuery(id+"F0.wireOp",EDGE,"E7.right")])],"isStart":true})],"blendedInto":[makeQuery(id+"F1.opExtrude","CAP_FACE",FACE,{"disambiguationData":[OSD([subQ1,sQuery(id+"F0.wireOp",EDGE,"E0.top"),subQ0,sQuery(id+"F0.wireOp",EDGE,"E0.right"),sQuery(id+"F0.wireOp",EDGE,"E1.bottom"),sQuery(id+"F0.wireOp",EDGE,"E1.top"),sQuery(id+"F0.wireOp",EDGE,"E2.bottom"),sQuery(id+"F0.wireOp",EDGE,"E2.top"),sQuery(id+"F0.wireOp",EDGE,"E2.left"),sQuery(id+"F0.wireOp",EDGE,"E2.right"),sQuery(id+"F0.wireOp",EDGE,"E3.left"),sQuery(id+"F0.wireOp",EDGE,"E3.right"),sQuery(id+"F0.wireOp",EDGE,"E4.bottom"),sQuery(id+"F0.wireOp",EDGE,"E4.top"),sQuery(id+"F0.wireOp",EDGE,"E4.left"),sQuery(id+"F0.wireOp",EDGE,"E4.right"),sQuery(id+"F0.wireOp",EDGE,"E5.bottom"),sQuery(id+"F0.wireOp",EDGE,"E5.top"),sQuery(id+"F0.wireOp",EDGE,"E6.bottom"),sQuery(id+"F0.wireOp",EDGE,"E6.top"),sQuery(id+"F0.wireOp",EDGE,"E6.left"),sQuery(id+"F0.wireOp",EDGE,"E6.right"),sQuery(id+"F0.wireOp",EDGE,"E7.left"),sQuery(id+"F0.wireOp",EDGE,"E7.right")])],"isStart":true})]});}
            var Q20;
            {var subQ0=sQuery(id+"F0.wireOp",EDGE,"E6.left");var subQ1=sQuery(id+"F0.wireOp",EDGE,"E6.top");Q20=makeQuery(id+"F2.opFillet","BLEND_EDGE",EDGE,{"blendedFrom":[makeQuery(id+"F1.opExtrude","SWEPT_EDGE",EDGE,{"disambiguationData":[OSD([subQ1,subQ0])]}),makeQuery(id+"F1.opExtrude","CAP_FACE",FACE,{"disambiguationData":[OSD([sQuery(id+"F0.wireOp",EDGE,"E0.bottom"),sQuery(id+"F0.wireOp",EDGE,"E0.top"),sQuery(id+"F0.wireOp",EDGE,"E0.left"),sQuery(id+"F0.wireOp",EDGE,"E0.right"),sQuery(id+"F0.wireOp",EDGE,"E1.bottom"),sQuery(id+"F0.wireOp",EDGE,"E1.top"),sQuery(id+"F0.wireOp",EDGE,"E2.bottom"),sQuery(id+"F0.wireOp",EDGE,"E2.top"),sQuery(id+"F0.wireOp",EDGE,"E2.left"),sQuery(id+"F0.wireOp",EDGE,"E2.right"),sQuery(id+"F0.wireOp",EDGE,"E3.left"),sQuery(id+"F0.wireOp",EDGE,"E3.right"),sQuery(id+"F0.wireOp",EDGE,"E4.bottom"),sQuery(id+"F0.wireOp",EDGE,"E4.top"),sQuery(id+"F0.wireOp",EDGE,"E4.left"),sQuery(id+"F0.wireOp",EDGE,"E4.right"),sQuery(id+"F0.wireOp",EDGE,"E5.bottom"),sQuery(id+"F0.wireOp",EDGE,"E5.top"),sQuery(id+"F0.wireOp",EDGE,"E6.bottom"),subQ1,subQ0,sQuery(id+"F0.wireOp",EDGE,"E6.right"),sQuery(id+"F0.wireOp",EDGE,"E7.left"),sQuery(id+"F0.wireOp",EDGE,"E7.right")])],"isStart":true})],"blendedInto":[makeQuery(id+"F1.opExtrude","CAP_FACE",FACE,{"disambiguationData":[OSD([sQuery(id+"F0.wireOp",EDGE,"E0.bottom"),sQuery(id+"F0.wireOp",EDGE,"E0.top"),sQuery(id+"F0.wireOp",EDGE,"E0.left"),sQuery(id+"F0.wireOp",EDGE,"E0.right"),sQuery(id+"F0.wireOp",EDGE,"E1.bottom"),sQuery(id+"F0.wireOp",EDGE,"E1.top"),sQuery(id+"F0.wireOp",EDGE,"E2.bottom"),sQuery(id+"F0.wireOp",EDGE,"E2.top"),sQuery(id+"F0.wireOp",EDGE,"E2.left"),sQuery(id+"F0.wireOp",EDGE,"E2.right"),sQuery(id+"F0.wireOp",EDGE,"E3.left"),sQuery(id+"F0.wireOp",EDGE,"E3.right"),sQuery(id+"F0.wireOp",EDGE,"E4.bottom"),sQuery(id+"F0.wireOp",EDGE,"E4.top"),sQuery(id+"F0.wireOp",EDGE,"E4.left"),sQuery(id+"F0.wireOp",EDGE,"E4.right"),sQuery(id+"F0.wireOp",EDGE,"E5.bottom"),sQuery(id+"F0.wireOp",EDGE,"E5.top"),sQuery(id+"F0.wireOp",EDGE,"E6.bottom"),subQ1,subQ0,sQuery(id+"F0.wireOp",EDGE,"E6.right"),sQuery(id+"F0.wireOp",EDGE,"E7.left"),sQuery(id+"F0.wireOp",EDGE,"E7.right")])],"isStart":true})]});}
            var Q21;
            Q21=makeQuery(id+"F1.opExtrude","CAP_EDGE",EDGE,{"disambiguationData":[OSD([sQuery(id+"F0.wireOp",EDGE,"E4.top"),sQuery(id+"F0.wireOp",EDGE,"E5.top"),sQuery(id+"F0.wireOp",EDGE,"E6.top")])],"isStart":true});
            var Q22;
            {var subQ0=sQuery(id+"F0.wireOp",EDGE,"E4.right");var subQ1=sQuery(id+"F0.wireOp",EDGE,"E4.top");Q22=makeQuery(id+"F2.opFillet","BLEND_EDGE",EDGE,{"blendedFrom":[makeQuery(id+"F1.opExtrude","SWEPT_EDGE",EDGE,{"disambiguationData":[OSD([subQ1,subQ0])]}),makeQuery(id+"F1.opExtrude","CAP_FACE",FACE,{"disambiguationData":[OSD([sQuery(id+"F0.wireOp",EDGE,"E0.bottom"),sQuery(id+"F0.wireOp",EDGE,"E0.top"),sQuery(id+"F0.wireOp",EDGE,"E0.left"),sQuery(id+"F0.wireOp",EDGE,"E0.right"),sQuery(id+"F0.wireOp",EDGE,"E1.bottom"),sQuery(id+"F0.wireOp",EDGE,"E1.top"),sQuery(id+"F0.wireOp",EDGE,"E2.bottom"),sQuery(id+"F0.wireOp",EDGE,"E2.top"),sQuery(id+"F0.wireOp",EDGE,"E2.left"),sQuery(id+"F0.wireOp",EDGE,"E2.right"),sQuery(id+"F0.wireOp",EDGE,"E3.left"),sQuery(id+"F0.wireOp",EDGE,"E3.right"),sQuery(id+"F0.wireOp",EDGE,"E4.bottom"),subQ1,sQuery(id+"F0.wireOp",EDGE,"E4.left"),subQ0,sQuery(id+"F0.wireOp",EDGE,"E5.bottom"),sQuery(id+"F0.wireOp",EDGE,"E5.top"),sQuery(id+"F0.wireOp",EDGE,"E6.bottom"),sQuery(id+"F0.wireOp",EDGE,"E6.top"),sQuery(id+"F0.wireOp",EDGE,"E6.left"),sQuery(id+"F0.wireOp",EDGE,"E6.right"),sQuery(id+"F0.wireOp",EDGE,"E7.left"),sQuery(id+"F0.wireOp",EDGE,"E7.right")])],"isStart":true})],"blendedInto":[makeQuery(id+"F1.opExtrude","CAP_FACE",FACE,{"disambiguationData":[OSD([sQuery(id+"F0.wireOp",EDGE,"E0.bottom"),sQuery(id+"F0.wireOp",EDGE,"E0.top"),sQuery(id+"F0.wireOp",EDGE,"E0.left"),sQuery(id+"F0.wireOp",EDGE,"E0.right"),sQuery(id+"F0.wireOp",EDGE,"E1.bottom"),sQuery(id+"F0.wireOp",EDGE,"E1.top"),sQuery(id+"F0.wireOp",EDGE,"E2.bottom"),sQuery(id+"F0.wireOp",EDGE,"E2.top"),sQuery(id+"F0.wireOp",EDGE,"E2.left"),sQuery(id+"F0.wireOp",EDGE,"E2.right"),sQuery(id+"F0.wireOp",EDGE,"E3.left"),sQuery(id+"F0.wireOp",EDGE,"E3.right"),sQuery(id+"F0.wireOp",EDGE,"E4.bottom"),subQ1,sQuery(id+"F0.wireOp",EDGE,"E4.left"),subQ0,sQuery(id+"F0.wireOp",EDGE,"E5.bottom"),sQuery(id+"F0.wireOp",EDGE,"E5.top"),sQuery(id+"F0.wireOp",EDGE,"E6.bottom"),sQuery(id+"F0.wireOp",EDGE,"E6.top"),sQuery(id+"F0.wireOp",EDGE,"E6.left"),sQuery(id+"F0.wireOp",EDGE,"E6.right"),sQuery(id+"F0.wireOp",EDGE,"E7.left"),sQuery(id+"F0.wireOp",EDGE,"E7.right")])],"isStart":true})]});}
            var Q23;
            Q23=makeQuery(id+"F1.opExtrude","CAP_EDGE",EDGE,{"disambiguationData":[OSD([sQuery(id+"F0.wireOp",EDGE,"E0.left"),sQuery(id+"F0.wireOp",EDGE,"E6.left"),sQuery(id+"F0.wireOp",EDGE,"E7.left")])],"isStart":true});
            var Q24;
            {var subQ0=sQuery(id+"F0.wireOp",EDGE,"E6.right");var subQ1=sQuery(id+"F0.wireOp",EDGE,"E6.bottom");Q24=makeQuery(id+"F3.opFillet","BLEND_EDGE",EDGE,{"blendedFrom":[makeQuery(id+"F1.opExtrude","SWEPT_EDGE",EDGE,{"disambiguationData":[OSD([subQ1,subQ0])]}),makeQuery(id+"F1.opExtrude","CAP_FACE",FACE,{"disambiguationData":[OSD([sQuery(id+"F0.wireOp",EDGE,"E0.bottom"),sQuery(id+"F0.wireOp",EDGE,"E0.top"),sQuery(id+"F0.wireOp",EDGE,"E0.left"),sQuery(id+"F0.wireOp",EDGE,"E0.right"),sQuery(id+"F0.wireOp",EDGE,"E1.bottom"),sQuery(id+"F0.wireOp",EDGE,"E1.top"),sQuery(id+"F0.wireOp",EDGE,"E2.bottom"),sQuery(id+"F0.wireOp",EDGE,"E2.top"),sQuery(id+"F0.wireOp",EDGE,"E2.left"),sQuery(id+"F0.wireOp",EDGE,"E2.right"),sQuery(id+"F0.wireOp",EDGE,"E3.left"),sQuery(id+"F0.wireOp",EDGE,"E3.right"),sQuery(id+"F0.wireOp",EDGE,"E4.bottom"),sQuery(id+"F0.wireOp",EDGE,"E4.top"),sQuery(id+"F0.wireOp",EDGE,"E4.left"),sQuery(id+"F0.wireOp",EDGE,"E4.right"),sQuery(id+"F0.wireOp",EDGE,"E5.bottom"),sQuery(id+"F0.wireOp",EDGE,"E5.top"),subQ1,sQuery(id+"F0.wireOp",EDGE,"E6.top"),sQuery(id+"F0.wireOp",EDGE,"E6.left"),subQ0,sQuery(id+"F0.wireOp",EDGE,"E7.left"),sQuery(id+"F0.wireOp",EDGE,"E7.right")])],"isStart":true})],"blendedInto":[makeQuery(id+"F1.opExtrude","CAP_FACE",FACE,{"disambiguationData":[OSD([sQuery(id+"F0.wireOp",EDGE,"E0.bottom"),sQuery(id+"F0.wireOp",EDGE,"E0.top"),sQuery(id+"F0.wireOp",EDGE,"E0.left"),sQuery(id+"F0.wireOp",EDGE,"E0.right"),sQuery(id+"F0.wireOp",EDGE,"E1.bottom"),sQuery(id+"F0.wireOp",EDGE,"E1.top"),sQuery(id+"F0.wireOp",EDGE,"E2.bottom"),sQuery(id+"F0.wireOp",EDGE,"E2.top"),sQuery(id+"F0.wireOp",EDGE,"E2.left"),sQuery(id+"F0.wireOp",EDGE,"E2.right"),sQuery(id+"F0.wireOp",EDGE,"E3.left"),sQuery(id+"F0.wireOp",EDGE,"E3.right"),sQuery(id+"F0.wireOp",EDGE,"E4.bottom"),sQuery(id+"F0.wireOp",EDGE,"E4.top"),sQuery(id+"F0.wireOp",EDGE,"E4.left"),sQuery(id+"F0.wireOp",EDGE,"E4.right"),sQuery(id+"F0.wireOp",EDGE,"E5.bottom"),sQuery(id+"F0.wireOp",EDGE,"E5.top"),subQ1,sQuery(id+"F0.wireOp",EDGE,"E6.top"),sQuery(id+"F0.wireOp",EDGE,"E6.left"),subQ0,sQuery(id+"F0.wireOp",EDGE,"E7.left"),sQuery(id+"F0.wireOp",EDGE,"E7.right")])],"isStart":true})]});}
            var Q25;
            {var subQ0=sQuery(id+"F0.wireOp",EDGE,"E4.left");var subQ1=sQuery(id+"F0.wireOp",EDGE,"E4.bottom");Q25=makeQuery(id+"F3.opFillet","BLEND_EDGE",EDGE,{"blendedFrom":[makeQuery(id+"F1.opExtrude","SWEPT_EDGE",EDGE,{"disambiguationData":[OSD([subQ1,subQ0])]}),makeQuery(id+"F1.opExtrude","CAP_FACE",FACE,{"disambiguationData":[OSD([sQuery(id+"F0.wireOp",EDGE,"E0.bottom"),sQuery(id+"F0.wireOp",EDGE,"E0.top"),sQuery(id+"F0.wireOp",EDGE,"E0.left"),sQuery(id+"F0.wireOp",EDGE,"E0.right"),sQuery(id+"F0.wireOp",EDGE,"E1.bottom"),sQuery(id+"F0.wireOp",EDGE,"E1.top"),sQuery(id+"F0.wireOp",EDGE,"E2.bottom"),sQuery(id+"F0.wireOp",EDGE,"E2.top"),sQuery(id+"F0.wireOp",EDGE,"E2.left"),sQuery(id+"F0.wireOp",EDGE,"E2.right"),sQuery(id+"F0.wireOp",EDGE,"E3.left"),sQuery(id+"F0.wireOp",EDGE,"E3.right"),subQ1,sQuery(id+"F0.wireOp",EDGE,"E4.top"),subQ0,sQuery(id+"F0.wireOp",EDGE,"E4.right"),sQuery(id+"F0.wireOp",EDGE,"E5.bottom"),sQuery(id+"F0.wireOp",EDGE,"E5.top"),sQuery(id+"F0.wireOp",EDGE,"E6.bottom"),sQuery(id+"F0.wireOp",EDGE,"E6.top"),sQuery(id+"F0.wireOp",EDGE,"E6.left"),sQuery(id+"F0.wireOp",EDGE,"E6.right"),sQuery(id+"F0.wireOp",EDGE,"E7.left"),sQuery(id+"F0.wireOp",EDGE,"E7.right")])],"isStart":true})],"blendedInto":[makeQuery(id+"F1.opExtrude","CAP_FACE",FACE,{"disambiguationData":[OSD([sQuery(id+"F0.wireOp",EDGE,"E0.bottom"),sQuery(id+"F0.wireOp",EDGE,"E0.top"),sQuery(id+"F0.wireOp",EDGE,"E0.left"),sQuery(id+"F0.wireOp",EDGE,"E0.right"),sQuery(id+"F0.wireOp",EDGE,"E1.bottom"),sQuery(id+"F0.wireOp",EDGE,"E1.top"),sQuery(id+"F0.wireOp",EDGE,"E2.bottom"),sQuery(id+"F0.wireOp",EDGE,"E2.top"),sQuery(id+"F0.wireOp",EDGE,"E2.left"),sQuery(id+"F0.wireOp",EDGE,"E2.right"),sQuery(id+"F0.wireOp",EDGE,"E3.left"),sQuery(id+"F0.wireOp",EDGE,"E3.right"),subQ1,sQuery(id+"F0.wireOp",EDGE,"E4.top"),subQ0,sQuery(id+"F0.wireOp",EDGE,"E4.right"),sQuery(id+"F0.wireOp",EDGE,"E5.bottom"),sQuery(id+"F0.wireOp",EDGE,"E5.top"),sQuery(id+"F0.wireOp",EDGE,"E6.bottom"),sQuery(id+"F0.wireOp",EDGE,"E6.top"),sQuery(id+"F0.wireOp",EDGE,"E6.left"),sQuery(id+"F0.wireOp",EDGE,"E6.right"),sQuery(id+"F0.wireOp",EDGE,"E7.left"),sQuery(id+"F0.wireOp",EDGE,"E7.right")])],"isStart":true})]});}
            var Q26;
            {var subQ0=sQuery(id+"F0.wireOp",EDGE,"E2.left");var subQ1=sQuery(id+"F0.wireOp",EDGE,"E2.top");Q26=makeQuery(id+"F3.opFillet","BLEND_EDGE",EDGE,{"blendedFrom":[makeQuery(id+"F1.opExtrude","SWEPT_EDGE",EDGE,{"disambiguationData":[OSD([subQ1,subQ0])]}),makeQuery(id+"F1.opExtrude","CAP_FACE",FACE,{"disambiguationData":[OSD([sQuery(id+"F0.wireOp",EDGE,"E0.bottom"),sQuery(id+"F0.wireOp",EDGE,"E0.top"),sQuery(id+"F0.wireOp",EDGE,"E0.left"),sQuery(id+"F0.wireOp",EDGE,"E0.right"),sQuery(id+"F0.wireOp",EDGE,"E1.bottom"),sQuery(id+"F0.wireOp",EDGE,"E1.top"),sQuery(id+"F0.wireOp",EDGE,"E2.bottom"),subQ1,subQ0,sQuery(id+"F0.wireOp",EDGE,"E2.right"),sQuery(id+"F0.wireOp",EDGE,"E3.left"),sQuery(id+"F0.wireOp",EDGE,"E3.right"),sQuery(id+"F0.wireOp",EDGE,"E4.bottom"),sQuery(id+"F0.wireOp",EDGE,"E4.top"),sQuery(id+"F0.wireOp",EDGE,"E4.left"),sQuery(id+"F0.wireOp",EDGE,"E4.right"),sQuery(id+"F0.wireOp",EDGE,"E5.bottom"),sQuery(id+"F0.wireOp",EDGE,"E5.top"),sQuery(id+"F0.wireOp",EDGE,"E6.bottom"),sQuery(id+"F0.wireOp",EDGE,"E6.top"),sQuery(id+"F0.wireOp",EDGE,"E6.left"),sQuery(id+"F0.wireOp",EDGE,"E6.right"),sQuery(id+"F0.wireOp",EDGE,"E7.left"),sQuery(id+"F0.wireOp",EDGE,"E7.right")])],"isStart":true})],"blendedInto":[makeQuery(id+"F1.opExtrude","CAP_FACE",FACE,{"disambiguationData":[OSD([sQuery(id+"F0.wireOp",EDGE,"E0.bottom"),sQuery(id+"F0.wireOp",EDGE,"E0.top"),sQuery(id+"F0.wireOp",EDGE,"E0.left"),sQuery(id+"F0.wireOp",EDGE,"E0.right"),sQuery(id+"F0.wireOp",EDGE,"E1.bottom"),sQuery(id+"F0.wireOp",EDGE,"E1.top"),sQuery(id+"F0.wireOp",EDGE,"E2.bottom"),subQ1,subQ0,sQuery(id+"F0.wireOp",EDGE,"E2.right"),sQuery(id+"F0.wireOp",EDGE,"E3.left"),sQuery(id+"F0.wireOp",EDGE,"E3.right"),sQuery(id+"F0.wireOp",EDGE,"E4.bottom"),sQuery(id+"F0.wireOp",EDGE,"E4.top"),sQuery(id+"F0.wireOp",EDGE,"E4.left"),sQuery(id+"F0.wireOp",EDGE,"E4.right"),sQuery(id+"F0.wireOp",EDGE,"E5.bottom"),sQuery(id+"F0.wireOp",EDGE,"E5.top"),sQuery(id+"F0.wireOp",EDGE,"E6.bottom"),sQuery(id+"F0.wireOp",EDGE,"E6.top"),sQuery(id+"F0.wireOp",EDGE,"E6.left"),sQuery(id+"F0.wireOp",EDGE,"E6.right"),sQuery(id+"F0.wireOp",EDGE,"E7.left"),sQuery(id+"F0.wireOp",EDGE,"E7.right")])],"isStart":true})]});}
            var Q27;
            {var subQ0=sQuery(id+"F0.wireOp",EDGE,"E0.right");var subQ1=sQuery(id+"F0.wireOp",EDGE,"E0.top");Q27=makeQuery(id+"F3.opFillet","BLEND_EDGE",EDGE,{"blendedFrom":[makeQuery(id+"F1.opExtrude","SWEPT_EDGE",EDGE,{"disambiguationData":[OSD([subQ1,subQ0])]}),makeQuery(id+"F1.opExtrude","CAP_FACE",FACE,{"disambiguationData":[OSD([sQuery(id+"F0.wireOp",EDGE,"E0.bottom"),subQ1,sQuery(id+"F0.wireOp",EDGE,"E0.left"),subQ0,sQuery(id+"F0.wireOp",EDGE,"E1.bottom"),sQuery(id+"F0.wireOp",EDGE,"E1.top"),sQuery(id+"F0.wireOp",EDGE,"E2.bottom"),sQuery(id+"F0.wireOp",EDGE,"E2.top"),sQuery(id+"F0.wireOp",EDGE,"E2.left"),sQuery(id+"F0.wireOp",EDGE,"E2.right"),sQuery(id+"F0.wireOp",EDGE,"E3.left"),sQuery(id+"F0.wireOp",EDGE,"E3.right"),sQuery(id+"F0.wireOp",EDGE,"E4.bottom"),sQuery(id+"F0.wireOp",EDGE,"E4.top"),sQuery(id+"F0.wireOp",EDGE,"E4.left"),sQuery(id+"F0.wireOp",EDGE,"E4.right"),sQuery(id+"F0.wireOp",EDGE,"E5.bottom"),sQuery(id+"F0.wireOp",EDGE,"E5.top"),sQuery(id+"F0.wireOp",EDGE,"E6.bottom"),sQuery(id+"F0.wireOp",EDGE,"E6.top"),sQuery(id+"F0.wireOp",EDGE,"E6.left"),sQuery(id+"F0.wireOp",EDGE,"E6.right"),sQuery(id+"F0.wireOp",EDGE,"E7.left"),sQuery(id+"F0.wireOp",EDGE,"E7.right")])],"isStart":true})],"blendedInto":[makeQuery(id+"F1.opExtrude","CAP_FACE",FACE,{"disambiguationData":[OSD([sQuery(id+"F0.wireOp",EDGE,"E0.bottom"),subQ1,sQuery(id+"F0.wireOp",EDGE,"E0.left"),subQ0,sQuery(id+"F0.wireOp",EDGE,"E1.bottom"),sQuery(id+"F0.wireOp",EDGE,"E1.top"),sQuery(id+"F0.wireOp",EDGE,"E2.bottom"),sQuery(id+"F0.wireOp",EDGE,"E2.top"),sQuery(id+"F0.wireOp",EDGE,"E2.left"),sQuery(id+"F0.wireOp",EDGE,"E2.right"),sQuery(id+"F0.wireOp",EDGE,"E3.left"),sQuery(id+"F0.wireOp",EDGE,"E3.right"),sQuery(id+"F0.wireOp",EDGE,"E4.bottom"),sQuery(id+"F0.wireOp",EDGE,"E4.top"),sQuery(id+"F0.wireOp",EDGE,"E4.left"),sQuery(id+"F0.wireOp",EDGE,"E4.right"),sQuery(id+"F0.wireOp",EDGE,"E5.bottom"),sQuery(id+"F0.wireOp",EDGE,"E5.top"),sQuery(id+"F0.wireOp",EDGE,"E6.bottom"),sQuery(id+"F0.wireOp",EDGE,"E6.top"),sQuery(id+"F0.wireOp",EDGE,"E6.left"),sQuery(id+"F0.wireOp",EDGE,"E6.right"),sQuery(id+"F0.wireOp",EDGE,"E7.left"),sQuery(id+"F0.wireOp",EDGE,"E7.right")])],"isStart":true})]});}
            var Q28;
            Q28=makeQuery(id+"F1.opExtrude","CAP_EDGE",EDGE,{"disambiguationData":[OSD([sQuery(id+"F0.wireOp",EDGE,"E8")])],"isStart":false});
            var Q29;
            Q29=makeQuery(id+"F1.opExtrude","CAP_EDGE",EDGE,{"disambiguationData":[OSD([sQuery(id+"F0.wireOp",EDGE,"E8")])],"isStart":true});
            chamfer(context, id + "F5", {"entities" : qUnion([Q0, Q1, Q2, Q3, Q4, Q5, Q6, Q7, Q8, Q9, Q10, Q11, Q12, Q13, Q14, Q15, Q16, Q17, Q18, Q19, Q20, Q21, Q22, Q23, Q24, Q25, Q26, Q27, Q28, Q29]), "width" : 0.1 * mm, "tangentPropagation" : true});
        }
    });
